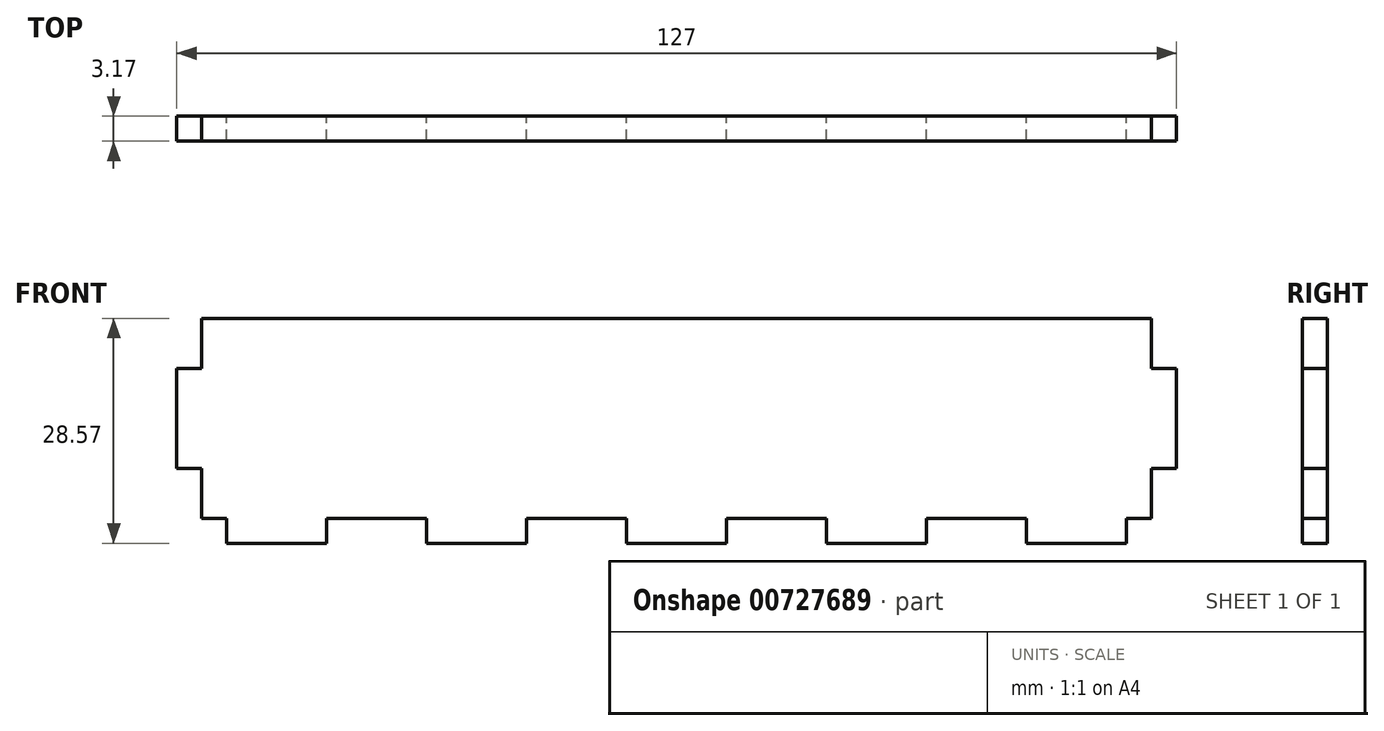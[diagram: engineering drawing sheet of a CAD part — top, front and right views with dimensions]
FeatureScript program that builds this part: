
annotation { "Feature Type Name" : "Feature", "Feature Type Description" : "" }
export const myFeature = defineFeature(function(context is Context, id is Id, definition is map)
    precondition{}
    {
        {
            var Q0;
            Q0=qCreatedBy(makeId("Front.planeOp"),FACE);
            var sketch = newSketch(context, id + "F0", { "sketchPlane" : qUnion([Q0])});
            skLineSegment(sketch, "E0.bottom", {"start": v(-104.85, 13.61) * mm, "end": v(15.8, 13.61) * mm});
            skLineSegment(sketch, "E0.top", {"start": v(-104.85, -11.79) * mm, "end": v(15.8, -11.79) * mm});
            skLineSegment(sketch, "E0.left", {"start": v(-104.85, 13.61) * mm, "end": v(-104.85, -11.79) * mm});
            skLineSegment(sketch, "E0.right", {"start": v(15.8, 13.61) * mm, "end": v(15.8, -11.79) * mm});
            skLineSegment(sketch, "E1", {"start": v(-104.85, -11.79) * mm, "end": v(-101.68, -11.79) * mm});
            skLineSegment(sketch, "E2", {"start": v(-101.68, -11.79) * mm, "end": v(-101.68, -14.96) * mm});
            skLineSegment(sketch, "E3", {"start": v(-101.68, -14.96) * mm, "end": v(-88.98, -14.96) * mm});
            skLineSegment(sketch, "E4", {"start": v(-88.98, -14.96) * mm, "end": v(-88.98, -11.79) * mm});
            skLineSegment(sketch, "E5", {"start": v(-88.98, -11.79) * mm, "end": v(-76.28, -11.79) * mm});
            skLineSegment(sketch, "E6", {"start": v(-76.28, -11.79) * mm, "end": v(-76.28, -14.96) * mm});
            skLineSegment(sketch, "E7", {"start": v(-76.28, -14.96) * mm, "end": v(-63.58, -14.96) * mm});
            skLineSegment(sketch, "E8", {"start": v(-63.58, -14.96) * mm, "end": v(-63.58, -11.79) * mm});
            skLineSegment(sketch, "E9", {"start": v(-63.58, -11.79) * mm, "end": v(-50.88, -11.79) * mm});
            skLineSegment(sketch, "E10", {"start": v(-50.88, -11.79) * mm, "end": v(-50.88, -14.96) * mm});
            skLineSegment(sketch, "E11", {"start": v(-50.88, -14.96) * mm, "end": v(-38.18, -14.96) * mm});
            skLineSegment(sketch, "E12", {"start": v(-38.18, -14.96) * mm, "end": v(-38.18, -11.79) * mm});
            skLineSegment(sketch, "E13", {"start": v(-38.18, -11.79) * mm, "end": v(-25.48, -11.79) * mm});
            skLineSegment(sketch, "E14", {"start": v(-25.48, -11.79) * mm, "end": v(-25.48, -14.96) * mm});
            skLineSegment(sketch, "E15", {"start": v(-25.48, -14.96) * mm, "end": v(-12.78, -14.96) * mm});
            skLineSegment(sketch, "E16", {"start": v(-12.78, -14.96) * mm, "end": v(-12.78, -11.79) * mm});
            skLineSegment(sketch, "E17", {"start": v(-12.78, -11.79) * mm, "end": v(-0.08, -11.79) * mm});
            skLineSegment(sketch, "E18", {"start": v(-0.08, -11.79) * mm, "end": v(-0.08, -14.96) * mm});
            skLineSegment(sketch, "E19", {"start": v(-0.08, -14.96) * mm, "end": v(12.62, -14.96) * mm});
            skLineSegment(sketch, "E20", {"start": v(12.62, -14.96) * mm, "end": v(12.62, -11.79) * mm});
            skLineSegment(sketch, "E21", {"start": v(12.62, -11.79) * mm, "end": v(25.32, -11.79) * mm});
            skLineSegment(sketch, "E22", {"start": v(-104.85, 13.61) * mm, "end": v(-104.85, 7.26) * mm});
            skLineSegment(sketch, "E23", {"start": v(-104.85, 7.26) * mm, "end": v(-108.03, 7.26) * mm});
            skLineSegment(sketch, "E24", {"start": v(-108.03, 7.26) * mm, "end": v(-108.03, -5.44) * mm});
            skLineSegment(sketch, "E25", {"start": v(-108.03, -5.44) * mm, "end": v(-104.85, -5.44) * mm});
            skLineSegment(sketch, "E26", {"start": v(15.8, 13.61) * mm, "end": v(15.8, 7.26) * mm});
            skLineSegment(sketch, "E27", {"start": v(15.8, 7.26) * mm, "end": v(18.97, 7.26) * mm});
            skLineSegment(sketch, "E28", {"start": v(18.97, 7.26) * mm, "end": v(18.97, -5.44) * mm});
            skLineSegment(sketch, "E29", {"start": v(18.97, -5.44) * mm, "end": v(15.8, -5.44) * mm});
            skSolve(sketch);
        }
        {
            var Q0;
            Q0=makeQuery(id+"F0.imprint","IMPRINT",FACE,{"disambiguationData":[TD([[makeQuery(id+"F0.imprint","IMPRINT",EDGE,{"derivedFrom":sQuery(id+"F0.wireOp",EDGE,"E0.bottom")}),-1.0]])]});
            var Q1;
            {var subQ0=sQuery(id+"F0.wireOp",EDGE,"E10");Q1=makeQuery(id+"F0.imprint","IMPRINT",FACE,{"disambiguationData":[TD([[makeQuery(id+"F0.imprint","IMPRINT",EDGE,{"derivedFrom":subQ0}),1.0]])]});}
            var Q2;
            {var subQ0=sQuery(id+"F0.wireOp",EDGE,"E14");Q2=makeQuery(id+"F0.imprint","IMPRINT",FACE,{"disambiguationData":[TD([[makeQuery(id+"F0.imprint","IMPRINT",EDGE,{"derivedFrom":subQ0}),1.0]])]});}
            var Q3;
            {var subQ0=sQuery(id+"F0.wireOp",EDGE,"E2");Q3=makeQuery(id+"F0.imprint","IMPRINT",FACE,{"disambiguationData":[TD([[makeQuery(id+"F0.imprint","IMPRINT",EDGE,{"derivedFrom":subQ0}),1.0]])]});}
            var Q4;
            {var subQ0=sQuery(id+"F0.wireOp",EDGE,"E6");Q4=makeQuery(id+"F0.imprint","IMPRINT",FACE,{"disambiguationData":[TD([[makeQuery(id+"F0.imprint","IMPRINT",EDGE,{"derivedFrom":subQ0}),1.0]])]});}
            var Q5;
            {var subQ0=sQuery(id+"F0.wireOp",EDGE,"E18");Q5=makeQuery(id+"F0.imprint","IMPRINT",FACE,{"disambiguationData":[TD([[makeQuery(id+"F0.imprint","IMPRINT",EDGE,{"derivedFrom":subQ0}),1.0]])]});}
            var Q6;
            {var subQ0=sQuery(id+"F0.wireOp",EDGE,"gVpqYOuL-59UL-0vWp-yV1u-nPBN169zkQMX");Q6=makeQuery(id+"F0.imprint","IMPRINT",FACE,{"disambiguationData":[TD([[makeQuery(id+"F0.imprint","IMPRINT",EDGE,{"derivedFrom":subQ0}),1.0]])]});}
            var Q7;
            {var subQ0=sQuery(id+"F0.wireOp",EDGE,"E23");Q7=makeQuery(id+"F0.imprint","IMPRINT",FACE,{"disambiguationData":[TD([[makeQuery(id+"F0.imprint","IMPRINT",EDGE,{"derivedFrom":subQ0}),1.0]])]});}
            var Q8;
            {var subQ0=sQuery(id+"F0.wireOp",EDGE,"E27");Q8=makeQuery(id+"F0.imprint","IMPRINT",FACE,{"disambiguationData":[TD([[makeQuery(id+"F0.imprint","IMPRINT",EDGE,{"derivedFrom":subQ0}),-1.0]])]});}
            extrude(context, id + "F1", {"entities" : qUnion([Q0, Q1, Q2, Q3, Q4, Q5, Q6, Q7, Q8]), "depth" : 3.17 * mm, "offsetDistance" : 25.4 * mm});
        }
    });
